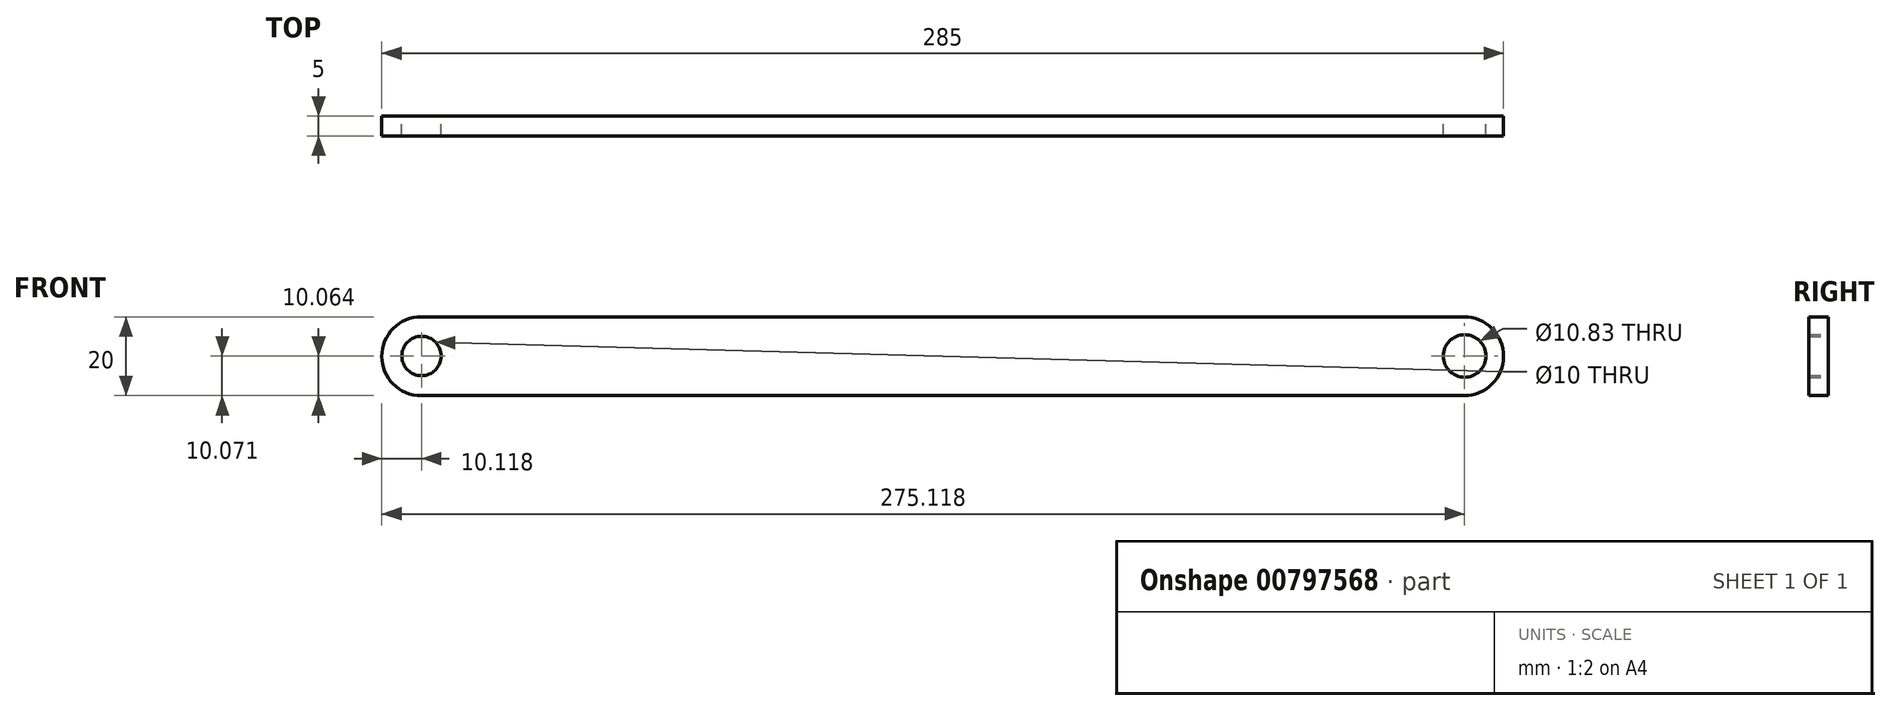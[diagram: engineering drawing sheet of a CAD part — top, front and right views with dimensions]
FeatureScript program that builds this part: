
annotation { "Feature Type Name" : "Feature", "Feature Type Description" : "" }
export const myFeature = defineFeature(function(context is Context, id is Id, definition is map)
    precondition{}
    {
        {
            var Q0;
            Q0=qCreatedBy(makeId("Front.planeOp"),FACE);
            var sketch = newSketch(context, id + "F0", { "sketchPlane" : qUnion([Q0])});
            skLineSegment(sketch, "E0.bottom", {"start": v(-285, 20) * mm, "end": v(0, 20) * mm});
            skLineSegment(sketch, "E0.top", {"start": v(-285, 0) * mm, "end": v(0, 0) * mm});
            skLineSegment(sketch, "E0.left", {"start": v(-285, 20) * mm, "end": v(-285, 0) * mm});
            skLineSegment(sketch, "E0.right", {"start": v(0, 20) * mm, "end": v(0, 0) * mm});
            skSolve(sketch);
        }
        {
            var Q0;
            Q0=makeQuery(id+"F0.imprint","IMPRINT",FACE,{"disambiguationData":[TD([[makeQuery(id+"F0.imprint","IMPRINT",EDGE,{"derivedFrom":sQuery(id+"F0.wireOp",EDGE,"E0.bottom")}),-1.0]])]});
            extrude(context, id + "F1", {"entities" : qUnion([Q0]), "depth" : 5 * mm, "offsetDistance" : 25 * mm});
        }
        {
            var Q0;
            Q0=makeQuery(id+"F1.opExtrude","SWEPT_EDGE",EDGE,{"disambiguationData":[OSD([sQuery(id+"F0.wireOp",EDGE,"E0.bottom"),sQuery(id+"F0.wireOp",EDGE,"E0.right")])]});
            var Q1;
            Q1=makeQuery(id+"F1.opExtrude","SWEPT_EDGE",EDGE,{"disambiguationData":[OSD([sQuery(id+"F0.wireOp",EDGE,"E0.top"),sQuery(id+"F0.wireOp",EDGE,"E0.right")])]});
            var Q2;
            Q2=makeQuery(id+"F1.opExtrude","SWEPT_EDGE",EDGE,{"disambiguationData":[OSD([sQuery(id+"F0.wireOp",EDGE,"E0.bottom"),sQuery(id+"F0.wireOp",EDGE,"E0.left")])]});
            var Q3;
            Q3=makeQuery(id+"F1.opExtrude","SWEPT_EDGE",EDGE,{"disambiguationData":[OSD([sQuery(id+"F0.wireOp",EDGE,"E0.top"),sQuery(id+"F0.wireOp",EDGE,"E0.left")])]});
            fillet(context, id + "F2", {"entities" : qUnion([Q0, Q1, Q2, Q3]), "radius" : 10 * mm, "tangentPropagation" : true, "allowEdgeOverflow" : false});
        }
        {
            var Q0;
            Q0=qCreatedBy(makeId("Front.planeOp"),FACE);
            var sketch = newSketch(context, id + "F3", { "sketchPlane" : qUnion([Q0])});
            skCircle(sketch, "E1", {"center": v(-274.88, 10.06) * mm, "radius": 5 * mm});
            skCircle(sketch, "E2", {"center": v(-9.88, 10.07) * mm, "radius": 5.41 * mm});
            skSolve(sketch);
        }
        {
            var Q0;
            Q0=qSketchRegion(id+"F3",true);
            extrude(context, id + "F4", {"entities" : qUnion([Q0]), "operationType" : NewBodyOperationType.REMOVE, "depth" : 20 * mm, "offsetDistance" : 25 * mm});
        }
    });
